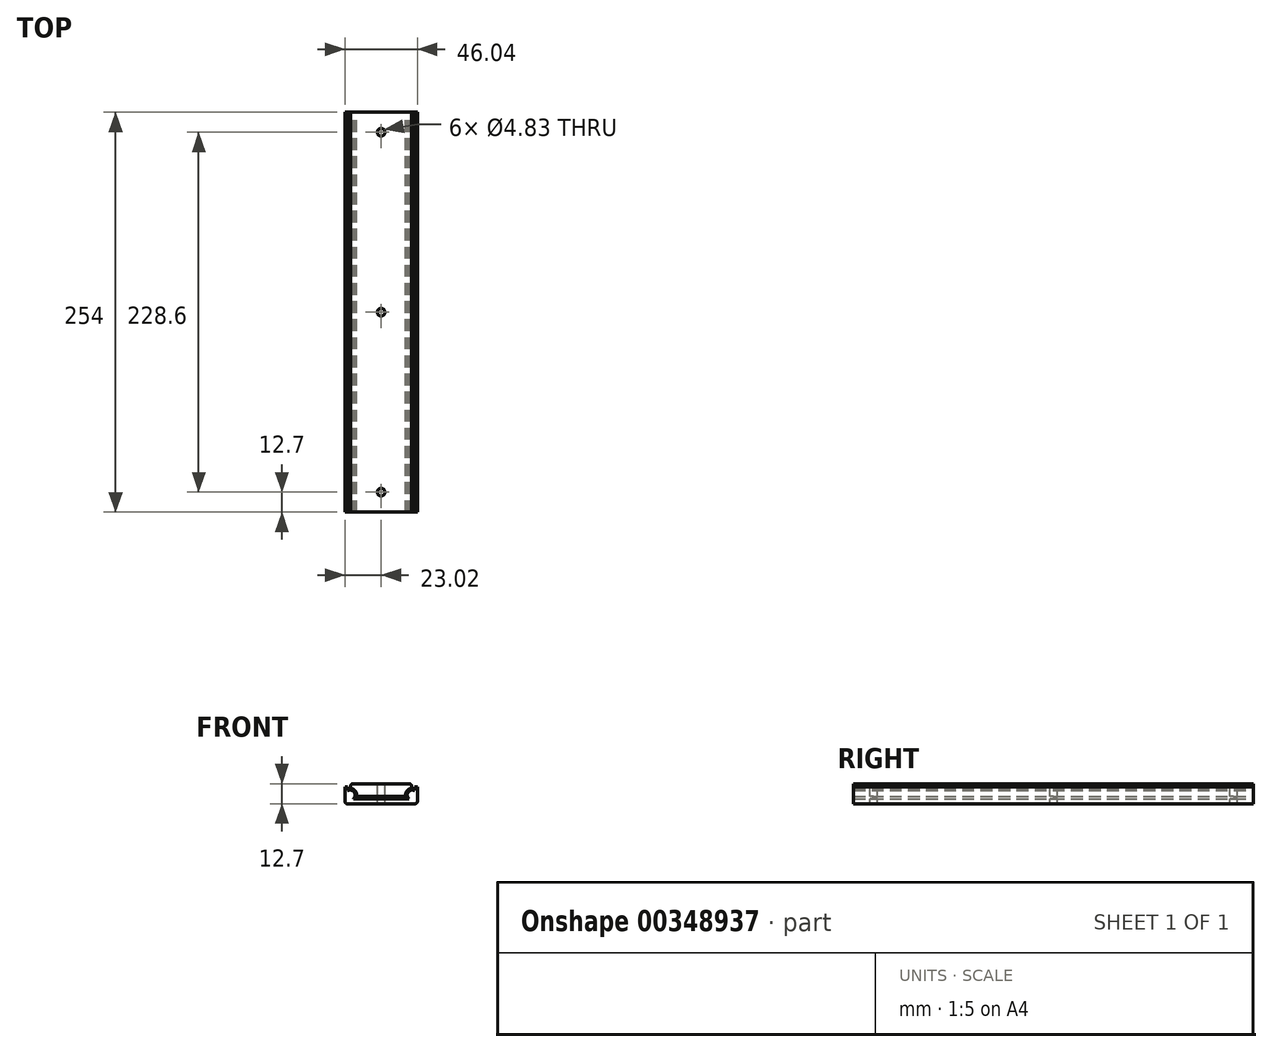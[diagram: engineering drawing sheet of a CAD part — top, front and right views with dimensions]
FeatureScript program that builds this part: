
annotation { "Feature Type Name" : "Feature", "Feature Type Description" : "" }
export const myFeature = defineFeature(function(context is Context, id is Id, definition is map)
    precondition{}
    {
        {
            var Q0;
            Q0=qCreatedBy(makeId("Front.planeOp"),FACE);
            var sketch = newSketch(context, id + "F0", { "sketchPlane" : qUnion([Q0])});
            skLineSegment(sketch, "E0", {"start": v(-23.02, 10.7) * mm, "end": v(-23.02, 1.52) * mm});
            skLineSegment(sketch, "E1", {"start": v(-21.5, 0) * mm, "end": v(21.5, 0) * mm});
            skLineSegment(sketch, "E2", {"start": v(23.02, 1.52) * mm, "end": v(23.02, 10.7) * mm});
            skLineSegment(sketch, "E3", {"start": v(-23.02, 10.7) * mm, "end": v(-21.18, 10.7) * mm});
            skLineSegment(sketch, "E4", {"start": v(-21.18, 10.7) * mm, "end": v(-21.18, 8.32) * mm});
            skLineSegment(sketch, "E5", {"start": v(-17.61, 3.1) * mm, "end": v(17.61, 3.1) * mm});
            skLineSegment(sketch, "E6", {"start": v(21.18, 8.32) * mm, "end": v(21.18, 10.7) * mm});
            skLineSegment(sketch, "E7", {"start": v(21.18, 10.7) * mm, "end": v(23.02, 10.7) * mm});
            skArc(sketch, "E8", {"start": v(-17.61, 3.1) * mm, "mid": v(-17.12, 7.26) * mm, "end": v(-21.18, 8.32) * mm});
            skArc(sketch, "E9", {"start": v(21.18, 8.32) * mm, "mid": v(17.12, 7.26) * mm, "end": v(17.61, 3.1) * mm});
            skArc(sketch, "E10", {"start": v(-15.59, 4.5) * mm, "mid": v(-16.29, 7.96) * mm, "end": v(-19.35, 9.72) * mm});
            skArc(sketch, "E11", {"start": v(19.35, 9.72) * mm, "mid": v(16.29, 7.96) * mm, "end": v(15.59, 4.5) * mm});
            skLineSegment(sketch, "E12", {"start": v(-19.35, 9.72) * mm, "end": v(-19.35, 11.18) * mm});
            skLineSegment(sketch, "E13", {"start": v(-17.83, 12.7) * mm, "end": v(17.83, 12.7) * mm});
            skLineSegment(sketch, "E14", {"start": v(19.35, 11.18) * mm, "end": v(19.35, 9.72) * mm});
            skLineSegment(sketch, "E15", {"start": v(15.59, 4.5) * mm, "end": v(-15.59, 4.5) * mm});
            skPoint(sketch, "E16.visualSharp", {"position": v(23.02, 0) * mm});
            skArc(sketch, "E16.filletArc", {"start": v(21.5, 0) * mm, "mid": v(22.57, 0.45) * mm, "end": v(23.02, 1.52) * mm});
            skPoint(sketch, "E17.visualSharp", {"position": v(-23.02, 0) * mm});
            skArc(sketch, "E17.filletArc", {"start": v(-23.02, 1.52) * mm, "mid": v(-22.57, 0.45) * mm, "end": v(-21.5, 0) * mm});
            skPoint(sketch, "E18.visualSharp", {"position": v(19.35, 12.7) * mm});
            skArc(sketch, "E18.filletArc", {"start": v(19.35, 11.18) * mm, "mid": v(18.9, 12.25) * mm, "end": v(17.83, 12.7) * mm});
            skPoint(sketch, "E19.visualSharp", {"position": v(-19.35, 12.7) * mm});
            skArc(sketch, "E19.filletArc", {"start": v(-17.83, 12.7) * mm, "mid": v(-18.9, 12.25) * mm, "end": v(-19.35, 11.18) * mm});
            skSolve(sketch);
        }
        {
            var Q0;
            Q0 = qSketchRegion(id + "F0", true);
            extrude(context, id + "F1", {"entities" : qUnion([Q0]), "depth" : 254 * mm});
        }
        {
            var Q0;
            Q0=qCreatedBy(makeId("Top.planeOp"),FACE);
            var sketch = newSketch(context, id + "F2", { "sketchPlane" : qUnion([Q0])});
            skCircle(sketch, "E20", {"center": v(0, -12.7) * mm, "radius": 2.41 * mm});
            skCircle(sketch, "E21", {"center": v(0, -127) * mm, "radius": 2.41 * mm});
            skCircle(sketch, "E22", {"center": v(0, -241.3) * mm, "radius": 2.41 * mm});
            skLineSegment(sketch, "E23", {"start": v(0, -12.7) * mm, "end": v(0, 0) * mm, "construction": true});
            skLineSegment(sketch, "E24", {"start": v(0, -241.3) * mm, "end": v(0, -254) * mm, "construction": true});
            skSolve(sketch);
        }
        {
            var Q0;
            Q0 = qSketchRegion(id + "F2", true);
            extrude(context, id + "F3", {"entities" : qUnion([Q0]), "operationType" : NewBodyOperationType.REMOVE, "endBound" : BoundingType.THROUGH_ALL, "oppositeDirection" : true, "depth" : 25.4 * mm, "hasSecondDirection" : true, "secondDirectionBound" : SecondDirectionBoundingType.THROUGH_ALL, "secondDirectionOppositeDirection" : false, "secondDirectionDepth" : 25.4 * mm});
        }
    });
